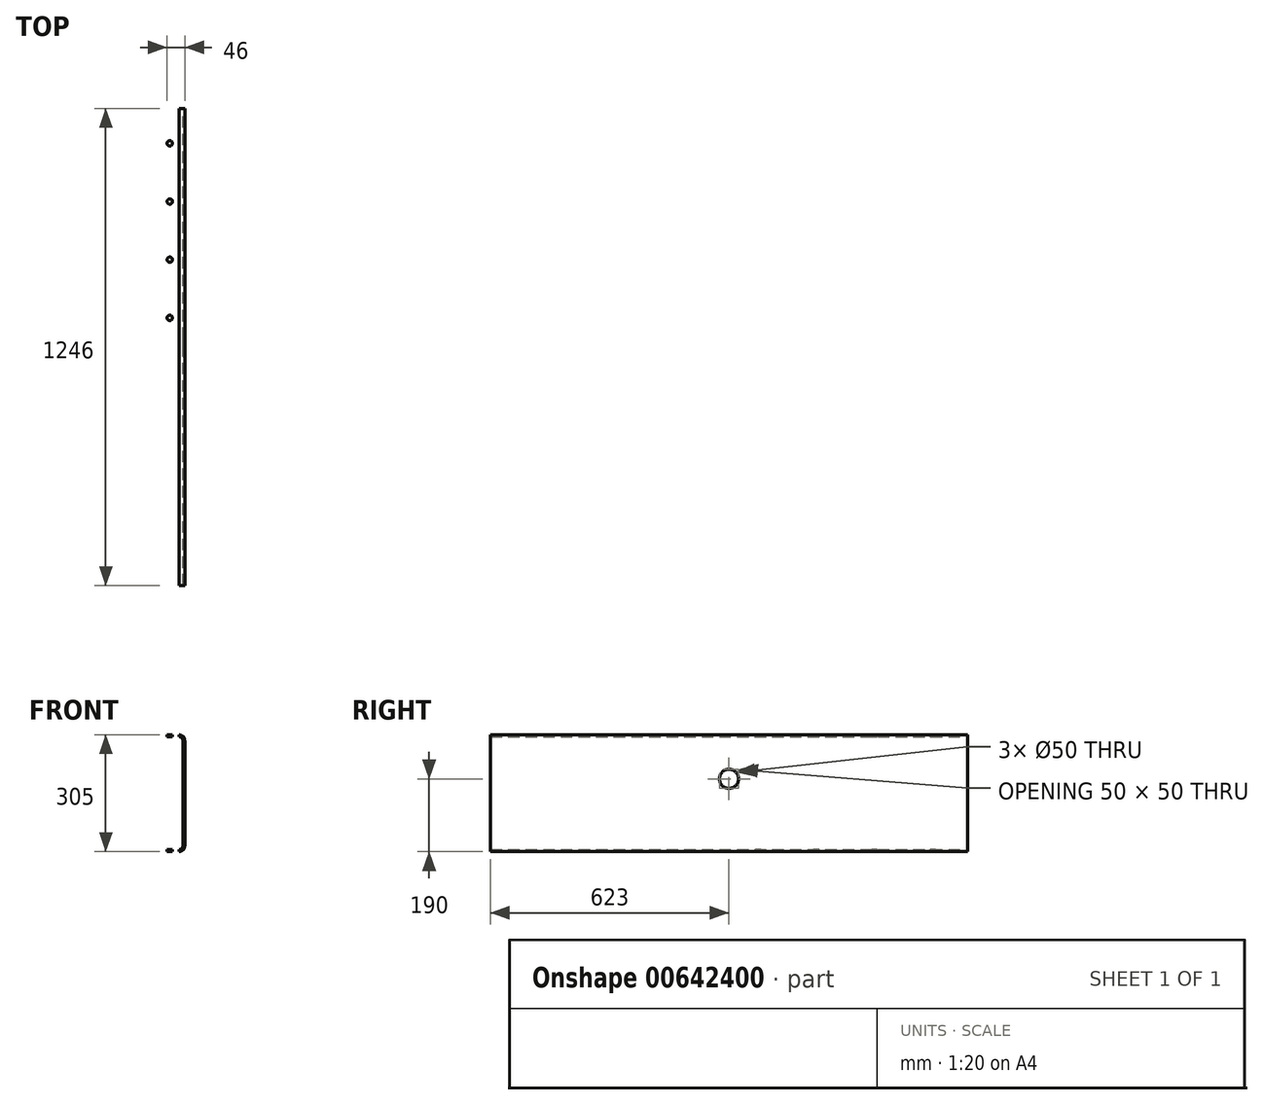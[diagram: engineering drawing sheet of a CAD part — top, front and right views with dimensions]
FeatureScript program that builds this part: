
annotation { "Feature Type Name" : "Feature", "Feature Type Description" : "" }
export const myFeature = defineFeature(function(context is Context, id is Id, definition is map)
    precondition{}
    {
        {
            var Q0;
            Q0=qCreatedBy(makeId("Front.planeOp"),FACE);
            var sketch = newSketch(context, id + "F0", { "sketchPlane" : qUnion([Q0])});
            skLineSegment(sketch, "E0.bottom", {"start": v(0, 0) * mm, "end": v(62, 0) * mm});
            skLineSegment(sketch, "E0.top", {"start": v(0, 305) * mm, "end": v(62, 305) * mm});
            skLineSegment(sketch, "E0.left", {"start": v(0, 0) * mm, "end": v(0, 5) * mm});
            skLineSegment(sketch, "E0.right", {"start": v(77, 15) * mm, "end": v(77, 290) * mm});
            skLineSegment(sketch, "E1.0", {"start": v(0, 5) * mm, "end": v(62, 5) * mm});
            skLineSegment(sketch, "E1.1", {"start": v(72, 15) * mm, "end": v(72, 290) * mm});
            skLineSegment(sketch, "E1.2", {"start": v(0, 300) * mm, "end": v(62, 300) * mm});
            skPoint(sketch, "E2.visualSharp", {"position": v(72, 300) * mm});
            skArc(sketch, "E2.filletArc", {"start": v(72, 290) * mm, "mid": v(69.07, 297.07) * mm, "end": v(62, 300) * mm});
            skPoint(sketch, "E3.visualSharp", {"position": v(72, 5) * mm});
            skArc(sketch, "E3.filletArc", {"start": v(62, 5) * mm, "mid": v(69.07, 7.93) * mm, "end": v(72, 15) * mm});
            skPoint(sketch, "E4.visualSharp", {"position": v(77, 0) * mm});
            skArc(sketch, "E4.filletArc", {"start": v(62, 0) * mm, "mid": v(72.6, 4.4) * mm, "end": v(77, 15) * mm});
            skPoint(sketch, "E5.visualSharp", {"position": v(77, 305) * mm});
            skArc(sketch, "E5.filletArc", {"start": v(77, 290) * mm, "mid": v(72.6, 300.6) * mm, "end": v(62, 305) * mm});
            skLineSegment(sketch, "E6.trimOffspring", {"start": v(0, 300) * mm, "end": v(0, 305) * mm});
            skSolve(sketch);
        }
        {
            var Q0;
            Q0=makeQuery(id+"F0.imprint","IMPRINT",FACE,{"disambiguationData":[TD([[makeQuery(id+"F0.imprint","IMPRINT",EDGE,{"derivedFrom":sQuery(id+"F0.wireOp",EDGE,"E0.bottom")}),1.0]])]});
            extrude(context, id + "F1", {"entities" : qUnion([Q0]), "depth" : 1246 * mm, "offsetDistance" : 25 * mm});
        }
        {
            var Q0;
            Q0=makeQuery(id+"F1.opExtrude","SWEPT_FACE",FACE,{"disambiguationData":[OSD([sQuery(id+"F0.wireOp",EDGE,"E0.right")])]});
            var sketch = newSketch(context, id + "F2", { "sketchPlane" : qUnion([Q0])});
            skLineSegment(sketch, "E7.0", {"start": v(-1246, 15) * mm, "end": v(-1246, 290) * mm});
            skLineSegment(sketch, "E8.0", {"start": v(-1246, 0) * mm, "end": v(0, 0) * mm});
            skLineSegment(sketch, "E9", {"start": v(-623, 0) * mm, "end": v(-623, 190) * mm, "construction": true});
            skPoint(sketch, "E9.endSnap0", {"position": v(-623, 15) * mm});
            skCircle(sketch, "E10", {"center": v(-623, 190) * mm, "radius": 25 * mm});
            skSolve(sketch);
        }
        {
            var Q0;
            Q0=makeQuery(id+"F2.imprint","IMPRINT",FACE,{"disambiguationData":[TD([[makeQuery(id+"F2.imprint","IMPRINT",EDGE,{"derivedFrom":sQuery(id+"F2.wireOp",EDGE,"E10")}),1.0]])]});
            extrude(context, id + "F3", {"entities" : qUnion([Q0]), "operationType" : NewBodyOperationType.REMOVE, "endBound" : BoundingType.UP_TO_NEXT, "oppositeDirection" : true, "depth" : 25 * mm, "offsetDistance" : 25 * mm});
        }
        {
            var Q0;
            Q0=makeQuery(id+"F1.opExtrude","SWEPT_FACE",FACE,{"disambiguationData":[OSD([sQuery(id+"F0.wireOp",EDGE,"E0.top")])]});
            var sketch = newSketch(context, id + "F4", { "sketchPlane" : qUnion([Q0])});
            skLineSegment(sketch, "E11", {"start": v(0, -623) * mm, "end": v(38, -623) * mm});
            skLineSegment(sketch, "E12.0", {"start": v(0, -699) * mm, "end": v(38, -699) * mm});
            skCircle(sketch, "E13", {"center": v(38, -699) * mm, "radius": 7 * mm});
            skCircle(sketch, "E14.0.1.0", {"center": v(38, -851) * mm, "radius": 7 * mm});
            skCircle(sketch, "E14.0.2.0", {"center": v(38, -1003) * mm, "radius": 7 * mm});
            skCircle(sketch, "E14.0.3.0", {"center": v(38, -1155) * mm, "radius": 7 * mm});
            skLineSegment(sketch, "E14.direction1", {"start": v(38, -699) * mm, "end": v(63, -699) * mm, "construction": true});
            skLineSegment(sketch, "E14.direction2", {"start": v(38, -699) * mm, "end": v(38, -851) * mm, "construction": true});
            skCircle(sketch, "E15.MirrorC", {"center": v(38, -547) * mm, "radius": 7 * mm});
            skCircle(sketch, "E16.MirrorC", {"center": v(38, -395) * mm, "radius": 7 * mm});
            skCircle(sketch, "E17.MirrorC", {"center": v(38, -243) * mm, "radius": 7 * mm});
            skCircle(sketch, "E18.MirrorC", {"center": v(38, -91) * mm, "radius": 7 * mm});
            skSolve(sketch);
        }
        {
            var Q0;
            Q0=makeQuery(id+"F4.imprint","IMPRINT",FACE,{"disambiguationData":[TD([[makeQuery(id+"F4.imprint","IMPRINT",EDGE,{"derivedFrom":sQuery(id+"F4.wireOp",EDGE,"E14.0.3.0")}),1.0]])]});
            var Q1;
            Q1=makeQuery(id+"F4.imprint","IMPRINT",FACE,{"disambiguationData":[TD([[makeQuery(id+"F4.imprint","IMPRINT",EDGE,{"derivedFrom":sQuery(id+"F4.wireOp",EDGE,"E14.0.2.0")}),1.0]])]});
            var Q2;
            Q2=makeQuery(id+"F4.imprint","IMPRINT",FACE,{"disambiguationData":[TD([[makeQuery(id+"F4.imprint","IMPRINT",EDGE,{"derivedFrom":sQuery(id+"F4.wireOp",EDGE,"E14.0.1.0")}),1.0]])]});
            var Q3;
            Q3=makeQuery(id+"F4.imprint","IMPRINT",FACE,{"disambiguationData":[TD([[makeQuery(id+"F4.imprint","IMPRINT",EDGE,{"derivedFrom":sQuery(id+"F4.wireOp",EDGE,"E13")}),1.0]])]});
            var Q4;
            Q4=makeQuery(id+"F4.imprint","IMPRINT",FACE,{"disambiguationData":[TD([[makeQuery(id+"F4.imprint","IMPRINT",EDGE,{"derivedFrom":sQuery(id+"F4.wireOp",EDGE,"E15.MirrorC")}),-1.0]])]});
            var Q5;
            Q5=makeQuery(id+"F4.imprint","IMPRINT",FACE,{"disambiguationData":[TD([[makeQuery(id+"F4.imprint","IMPRINT",EDGE,{"derivedFrom":sQuery(id+"F4.wireOp",EDGE,"E16.MirrorC")}),-1.0]])]});
            var Q6;
            Q6=makeQuery(id+"F4.imprint","IMPRINT",FACE,{"disambiguationData":[TD([[makeQuery(id+"F4.imprint","IMPRINT",EDGE,{"derivedFrom":sQuery(id+"F4.wireOp",EDGE,"E17.MirrorC")}),-1.0]])]});
            var Q7;
            Q7=makeQuery(id+"F4.imprint","IMPRINT",FACE,{"disambiguationData":[TD([[makeQuery(id+"F4.imprint","IMPRINT",EDGE,{"derivedFrom":sQuery(id+"F4.wireOp",EDGE,"E18.MirrorC")}),-1.0]])]});
            extrude(context, id + "F5", {"entities" : qUnion([Q0, Q1, Q2, Q3, Q4, Q5, Q6, Q7]), "operationType" : NewBodyOperationType.REMOVE, "endBound" : BoundingType.THROUGH_ALL, "oppositeDirection" : true, "depth" : 25 * mm, "offsetDistance" : 25 * mm});
        }
    });
